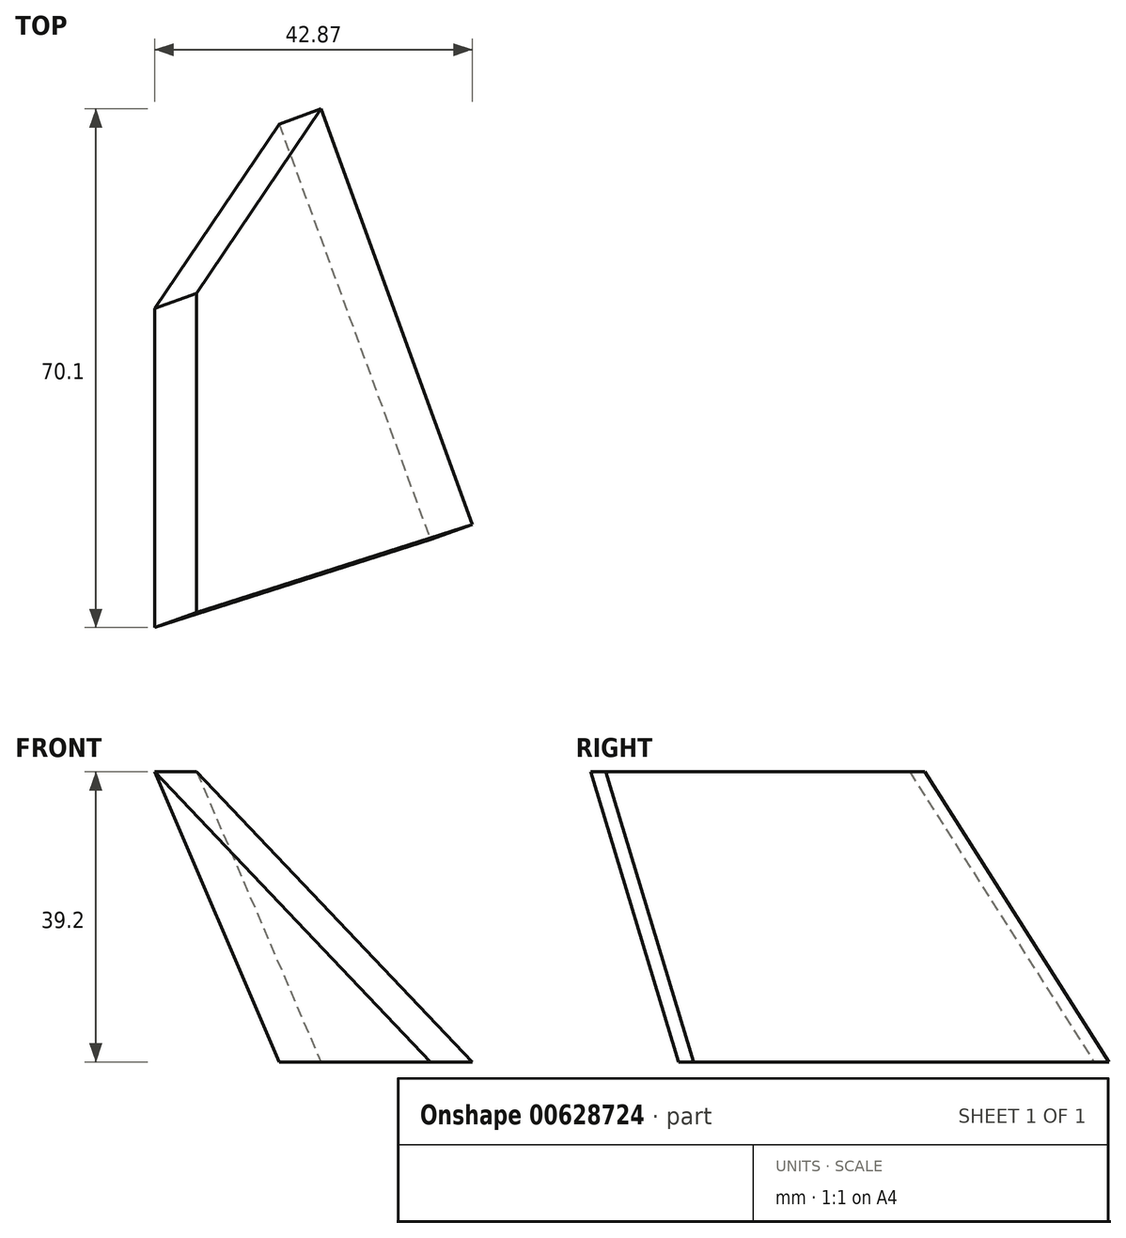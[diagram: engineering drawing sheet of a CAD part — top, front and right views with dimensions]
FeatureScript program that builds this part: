
annotation { "Feature Type Name" : "Feature", "Feature Type Description" : "" }
export const myFeature = defineFeature(function(context is Context, id is Id, definition is map)
    precondition{}
    {
        {
            var Q0;
            Q0=qCreatedBy(makeId("Front.planeOp"),FACE);
            var sketch = newSketch(context, id + "F0", { "sketchPlane" : qUnion([Q0])});
            skLineSegment(sketch, "E0", {"start": v(0, 0) * mm, "end": v(0, 71.35) * mm, "construction": true});
            skSolve(sketch);
        }
        {
            var Q0;
            Q0=sQuery(id+"F0.wireOp",EDGE,"E0");
            cPlane(context, id + "F1", {"entities" : qUnion([Q0]), "cplaneType" : CPlaneType.LINE_ANGLE, "offset" : 25.4 * mm, "angle" : 200 * degree, "width" : 152.4 * mm, "height" : 152.4 * mm});
        }
        {
            var Q0;
            Q0=sQuery(id+"F0.wireOp",EDGE,"E0");
            cPlane(context, id + "F2", {"entities" : qUnion([Q0]), "cplaneType" : CPlaneType.LINE_ANGLE, "offset" : 25.4 * mm, "angle" : 200 * degree, "oppositeDirection" : true, "width" : 152.4 * mm, "height" : 152.4 * mm});
        }
        {
            var Q0;
            Q0=qCreatedBy(makeId("Top.planeOp"),FACE);
            var sketch = newSketch(context, id + "F3", { "sketchPlane" : qUnion([Q0])});
            skLineSegment(sketch, "E1", {"start": v(0, 0) * mm, "end": v(76.2, 0) * mm, "construction": true});
            skLineSegment(sketch, "E2", {"start": v(82.8, 31.18) * mm, "end": v(82.8, -31.78) * mm});
            skSolve(sketch);
        }
        {
            var Q0;
            Q0=qCreatedBy(id+"F2.planeOp",FACE);
            var sketch = newSketch(context, id + "F4", { "sketchPlane" : qUnion([Q0])});
            skArc(sketch, "E3", {"start": v(85.91, -0.87) * mm, "mid": v(95.88, -10) * mm, "end": v(105.84, -0.87) * mm});
            skLineSegment(sketch, "E4", {"start": v(65.99, 227.4) * mm, "end": v(85.91, -0.87) * mm});
            skLineSegment(sketch, "E5", {"start": v(125.76, 227.4) * mm, "end": v(105.84, -0.87) * mm});
            skLineSegment(sketch, "E6", {"start": v(65.99, 227.4) * mm, "end": v(125.76, 227.4) * mm});
            skSolve(sketch);
        }
        {
            var Q0;
            Q0=qCreatedBy(id+"F1.planeOp",FACE);
            var sketch = newSketch(context, id + "F5", { "sketchPlane" : qUnion([Q0])});
            skArc(sketch, "E7", {"start": v(-140.4, 0) * mm, "mid": v(-130.44, -9.13) * mm, "end": v(-120.48, 0) * mm});
            skLineSegment(sketch, "E8", {"start": v(-160.32, 228.26) * mm, "end": v(-140.4, 0) * mm});
            skLineSegment(sketch, "E9", {"start": v(-100.55, 228.26) * mm, "end": v(-120.48, 0) * mm});
            skLineSegment(sketch, "E10", {"start": v(-160.32, 228.26) * mm, "end": v(-100.55, 228.26) * mm});
            skSolve(sketch);
        }
        {
            var Q0;
            Q0=sQuery(id+"F3.wireOp",EDGE,"E2");
            cPlane(context, id + "F6", {"entities" : qUnion([Q0]), "cplaneType" : CPlaneType.LINE_ANGLE, "offset" : 25 * mm, "angle" : 120 * degree, "width" : 150 * mm, "height" : 150 * mm});
        }
        {
            var Q0;
            Q0=qCreatedBy(id+"F6.planeOp",FACE);
            var sketch = newSketch(context, id + "F7", { "sketchPlane" : qUnion([Q0])});
            skArc(sketch, "E11", {"start": v(125.73, 267.44) * mm, "mid": v(16.78, 376.38) * mm, "end": v(-92.16, 267.44) * mm});
            skArc(sketch, "E12", {"start": v(82.61, 267.44) * mm, "mid": v(16.78, 333.27) * mm, "end": v(-49.04, 267.44) * mm});
            skLineSegment(sketch, "E13", {"start": v(82.61, 267.44) * mm, "end": v(125.73, 267.44) * mm});
            skLineSegment(sketch, "E14.trimOffspring", {"start": v(-49.04, 267.44) * mm, "end": v(-92.16, 267.44) * mm});
            skSolve(sketch);
        }
        {
            var Q0;
            Q0=makeQuery(id+"F5.imprint","IMPRINT",FACE,{"disambiguationData":[TD([[makeQuery(id+"F5.imprint","IMPRINT",EDGE,{"derivedFrom":sQuery(id+"F5.wireOp",EDGE,"E7")}),1.0]])]});
            var Q1;
            Q1=sQuery(id+"F5.wireOp",EDGE,"E7");
            var Q2;
            Q2=sQuery(id+"F5.wireOp",EDGE,"E8");
            var Q3;
            Q3=sQuery(id+"F5.wireOp",EDGE,"E9");
            var Q4;
            Q4=sQuery(id+"F5.wireOp",EDGE,"E10");
            var Q5;
            Q5=sQuery(id+"F4.wireOp",EDGE,"E3");
            var Q6;
            Q6=sQuery(id+"F4.wireOp",EDGE,"E4");
            var Q7;
            Q7=sQuery(id+"F4.wireOp",EDGE,"E5");
            var Q8;
            Q8=sQuery(id+"F4.wireOp",EDGE,"E6");
            var Q9;
            Q9=sQuery(id+"F7.wireOp",EDGE,"E12");
            var Q10;
            Q10=sQuery(id+"F7.wireOp",EDGE,"E14.trimOffspring");
            var Q11;
            Q11=sQuery(id+"F7.wireOp",EDGE,"E11");
            var Q12;
            Q12=sQuery(id+"F7.wireOp",EDGE,"E13");
            extrude(context, id + "F8", {"entities" : qUnion([Q0]), "bodyType" : ToolBodyType.SURFACE, "surfaceEntities" : qUnion([Q1, Q2, Q3, Q4, Q5, Q6, Q7, Q8, Q9, Q10, Q11, Q12]), "depth" : 6 * mm, "offsetDistance" : 25 * mm});
        }
        {
            var Q0;
            Q0=makeQuery(id+"F8.opExtrude","SWEPT_BODY",BODY,{"disambiguationData":[OSD([sQuery(id+"F7.wireOp",EDGE,"E13")])]});
            var Q1;
            Q1=makeQuery(id+"F8.opExtrude","SWEPT_BODY",BODY,{"disambiguationData":[OSD([sQuery(id+"F4.wireOp",EDGE,"E4")])]});
            var Q2;
            Q2=makeQuery(id+"F8.opExtrude","SWEPT_FACE",FACE,{"disambiguationData":[OSD([sQuery(id+"F4.wireOp",EDGE,"E6")])]});
            var Q3;
            Q3=makeQuery(id+"F8.opExtrude","SWEPT_FACE",FACE,{"disambiguationData":[OSD([sQuery(id+"F7.wireOp",EDGE,"E14.trimOffspring")])]});
            loft(context, id + "F9", {"bodyType" : ToolBodyType.SURFACE, "sheetProfilesArray" : [{ "sheetProfileEntities" : qUnion([Q0]) }, { "sheetProfileEntities" : qUnion([Q1]) }], "wireProfilesArray" : [{ "wireProfileEntities" : qUnion([Q2]) }, { "wireProfileEntities" : qUnion([Q3]) }]});
        }
        {
            var Q0;
            Q0=makeQuery(id+"F8.opExtrude","SWEPT_FACE",FACE,{"disambiguationData":[OSD([sQuery(id+"F7.wireOp",EDGE,"E13")])]});
            var Q1;
            Q1=makeQuery(id+"F8.opExtrude","SWEPT_FACE",FACE,{"disambiguationData":[OSD([sQuery(id+"F5.wireOp",EDGE,"E10")])]});
            loft(context, id + "F10", {"sheetProfilesArray" : [{ "sheetProfileEntities" : qUnion([Q0]) }, { "sheetProfileEntities" : qUnion([Q1]) }]});
        }
    });
